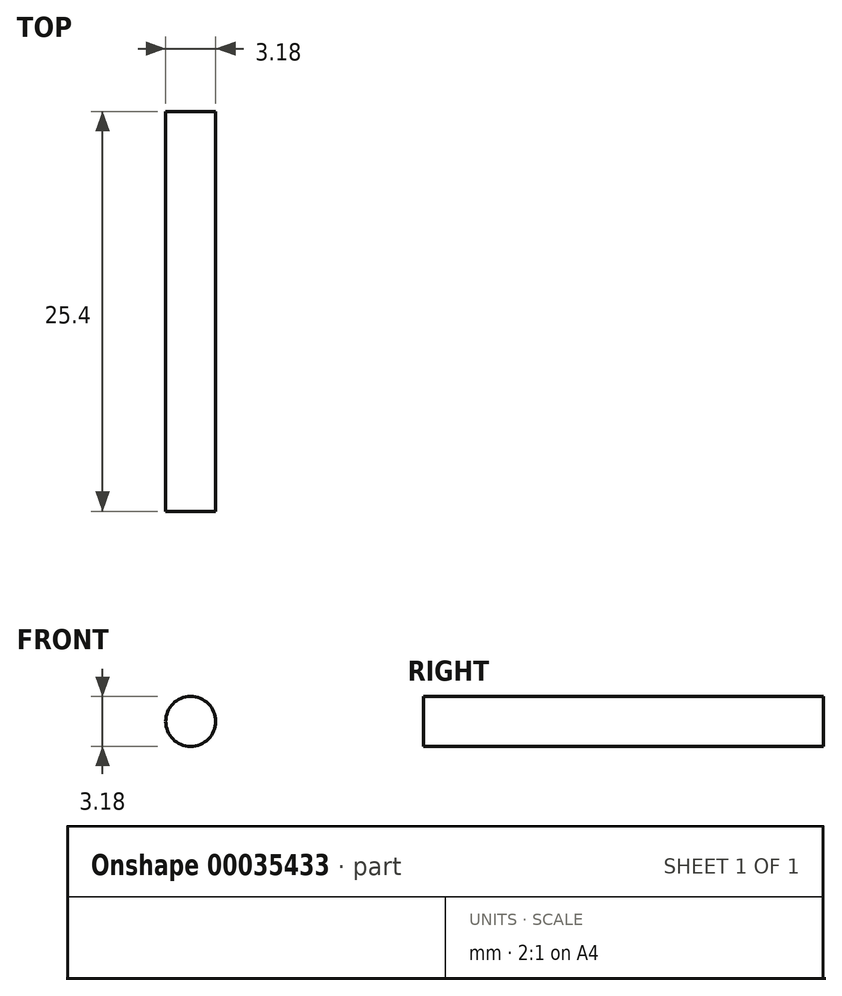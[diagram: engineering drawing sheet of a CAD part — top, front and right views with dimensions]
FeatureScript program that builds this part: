
annotation { "Feature Type Name" : "Feature", "Feature Type Description" : "" }
export const myFeature = defineFeature(function(context is Context, id is Id, definition is map)
    precondition{}
    {
        {
            var Q0;
            Q0=qCreatedBy(makeId("Front.planeOp"),FACE);
            var sketch = newSketch(context, id + "F0", { "sketchPlane" : qUnion([Q0])});
            skCircle(sketch, "E0", {"center": v(0, 0) * mm, "radius": 1.59 * mm});
            skSolve(sketch);
        }
        {
            var Q0;
            Q0 = qSketchRegion(id + "F0", true);
            extrude(context, id + "F1", {"entities" : qUnion([Q0]), "depth" : 25.4 * mm});
        }
    });
